# Revit family: Edge_TB42_A_Side_Hung_Standard
name_source: partatom
category: Windows
revit_build: Autodesk Revit 2014 (Build: 20130308_1515(x64)
units: mm (PartAtom-declared; Revit-internal decimal feet)

## types (6) — shared parameters
Aluminium Thickness = 1 mm  [stored 0.00328084 ft]
Bead SG Gap = 13 mm
Casement Dimension = 42 mm  [stored 0.137795 ft]
Custom Window Width = 590 mm  [stored 1.9357 ft]
DG Extrusion Start = 11 mm  [stored 0.0360892 ft]
DG Gasket Finish = Double Glazing Gasket Material
DG Thickness Calc = 4 mm  [stored 0.0131234 ft]
Default Sill Height = 800 mm  [stored 2.62467 ft]
Depth Bead = 28 mm  [stored 0.0918635 ft]
Description = Thermal break casement windows (42mm), Type A side hung
Frame Center Offset = 21 mm  [stored 0.0688976 ft]
Limit Sash Height Max = 1500 mm  [stored 4.92126 ft]
Limit Sash Height Min = 300 mm  [stored 0.984252 ft]
Limit Sash Width Max = 700 mm  [stored 2.29659 ft]
Limit Sash Width Min = 300 mm  [stored 0.984252 ft]
Limit Window Height Max = 1546 mm  [stored 5.07218 ft]
Limit Window Height Min = 346 mm
Limit Window Width Max = 746 mm  [stored 2.44751 ft]
Limit Window Width Min = 346 mm
Manufacturer = Crealco
Max System DG One Piece Thickness = 6 mm  [stored 0.019685 ft]
Max System DG Unit Thickness = 25 mm  [stored 0.082021 ft]
Model = Edge
Offset Bead SG Center Reversed = 21 mm  [stored 0.0688976 ft]
Offset Sash 1 Top = 23 mm  [stored 0.0754593 ft]
Offset Sash Left = 23 mm  [stored 0.0754593 ft]
Offset Window Exterior = 21 mm  [stored 0.0688976 ft]
SG Gasket Thickness = 6 mm  [stored 0.019685 ft]
Sash Center Offset = 18 mm
Sash Overlap = 7 mm  [stored 0.0229659 ft]
Sash Spacing Inner = 8 mm  [stored 0.0262467 ft]
Sash Width = 544 mm  [stored 1.78478 ft]
URL = http://www.crealco.co.za
Wall Closure = By host
Width = 590 mm  [stored 1.9357 ft]
Width Bead = 15 mm  [stored 0.0492126 ft]
Width Profile = 30 mm  [stored 0.0984252 ft]
Width Sash = 514 mm
Width Sash Opening = 544 mm  [stored 1.78478 ft]
zero-valued in all types: Window Exterior Offset

## per-type parameters (varying)
| type | Clearvue Insulated LowE SHGC Value | Clearvue Insulated LowE U Value | Clearvue Insulated SHGC Value | Clearvue Insulated U Value | Clearvue SHGC Value | Clearvue U Value | Custom Windload | Custom Window Height | Energy Advantage SHGC Value | Energy Advantage U Value | Height | Height Sash | Height Sash 1 Opening | Intruderprufe Insulated LowE SHGC Value | Intruderprufe Insulated LowE U Value | Intruderprufe Insulated SHGC Value | Intruderprufe Insulated U Value | Intruderprufe LowE SHGC Value | Intruderprufe LowE U Value | Intruderprufe SHGC Value | Intruderprufe U Value | Max Pane Area | Sash Height | Windload Design |
| EDGE-0609S-1000Pa | 0.41 | 2.77 | 0.45 | 3.2 | 0.492 | 5.13 | 1000 mm  [stored 3.28084 ft] | 890 mm  [stored 2.91995 ft] | 0.441 | 3.94 | 890 mm  [stored 2.91995 ft] | 814 mm  [stored 2.6706 ft] | 844 mm  [stored 2.76903 ft] | 0.372 | 2.73 | 0.413 | 3.15 | 0.413 | 3.93 | 0.459 | 5.04 | 0.37 m² | 844 mm  [stored 2.76903 ft] | 1000 mm  [stored 3.28084 ft] |
| EDGE-0612S-1000Pa | 0.431 | 2.7 | 0.474 | 3.16 | 0.52 | 5.2 | 1000 mm  [stored 3.28084 ft] | 1190 mm  [stored 3.9042 ft] | 0.466 | 3.92 | 1190 mm  [stored 3.9042 ft] | 1114 mm  [stored 3.65486 ft] | 1144 mm | 0.392 | 2.66 | 0.435 | 3.11 | 0.437 | 3.9 | 0.486 | 5.09 | 0.51 m² | 1144 mm | 1000 mm  [stored 3.28084 ft] |
| EDGE-0609S-1500Pa | 0.41 | 2.77 | 0.45 | 3.2 | 0.492 | 5.13 | 1500 mm  [stored 4.92126 ft] | 890 mm  [stored 2.91995 ft] | 0.441 | 3.94 | 890 mm  [stored 2.91995 ft] | 814 mm  [stored 2.6706 ft] | 844 mm  [stored 2.76903 ft] | 0.372 | 2.73 | 0.413 | 3.15 | 0.413 | 3.93 | 0.459 | 5.04 | 0.37 m² | 844 mm  [stored 2.76903 ft] | 1500 mm  [stored 4.92126 ft] |
| EDGE-0609S-2000Pa | 0.41 | 2.77 | 0.45 | 3.2 | 0.492 | 5.13 | 2000 mm  [stored 6.56168 ft] | 890 mm  [stored 2.91995 ft] | 0.441 | 3.94 | 890 mm  [stored 2.91995 ft] | 814 mm  [stored 2.6706 ft] | 844 mm  [stored 2.76903 ft] | 0.372 | 2.73 | 0.413 | 3.15 | 0.413 | 3.93 | 0.459 | 5.04 | 0.37 m² | 844 mm  [stored 2.76903 ft] | 2000 mm  [stored 6.56168 ft] |
| EDGE-0612S-1500Pa | 0.431 | 2.7 | 0.474 | 3.16 | 0.52 | 5.2 | 1500 mm  [stored 4.92126 ft] | 1190 mm  [stored 3.9042 ft] | 0.466 | 3.92 | 1190 mm  [stored 3.9042 ft] | 1114 mm  [stored 3.65486 ft] | 1144 mm | 0.392 | 2.66 | 0.435 | 3.11 | 0.437 | 3.9 | 0.486 | 5.09 | 0.51 m² | 1144 mm | 1500 mm  [stored 4.92126 ft] |
| EDGE-0612S-2000Pa | 0.431 | 2.7 | 0.474 | 3.16 | 0.52 | 5.2 | 2000 mm  [stored 6.56168 ft] | 1190 mm  [stored 3.9042 ft] | 0.466 | 3.92 | 1190 mm  [stored 3.9042 ft] | 1114 mm  [stored 3.65486 ft] | 1144 mm | 0.392 | 2.66 | 0.435 | 3.11 | 0.437 | 3.9 | 0.486 | 5.09 | 0.51 m² | 1144 mm | 2000 mm  [stored 6.56168 ft] |

note: [stored X ft] marks values corroborated as IEEE doubles in the binary element streams (Revit-internal decimal feet)

## geometry (parser evidence)
native form markers: Extrusion x1, Sweep x30
no freeform markers — native parametric forms only
